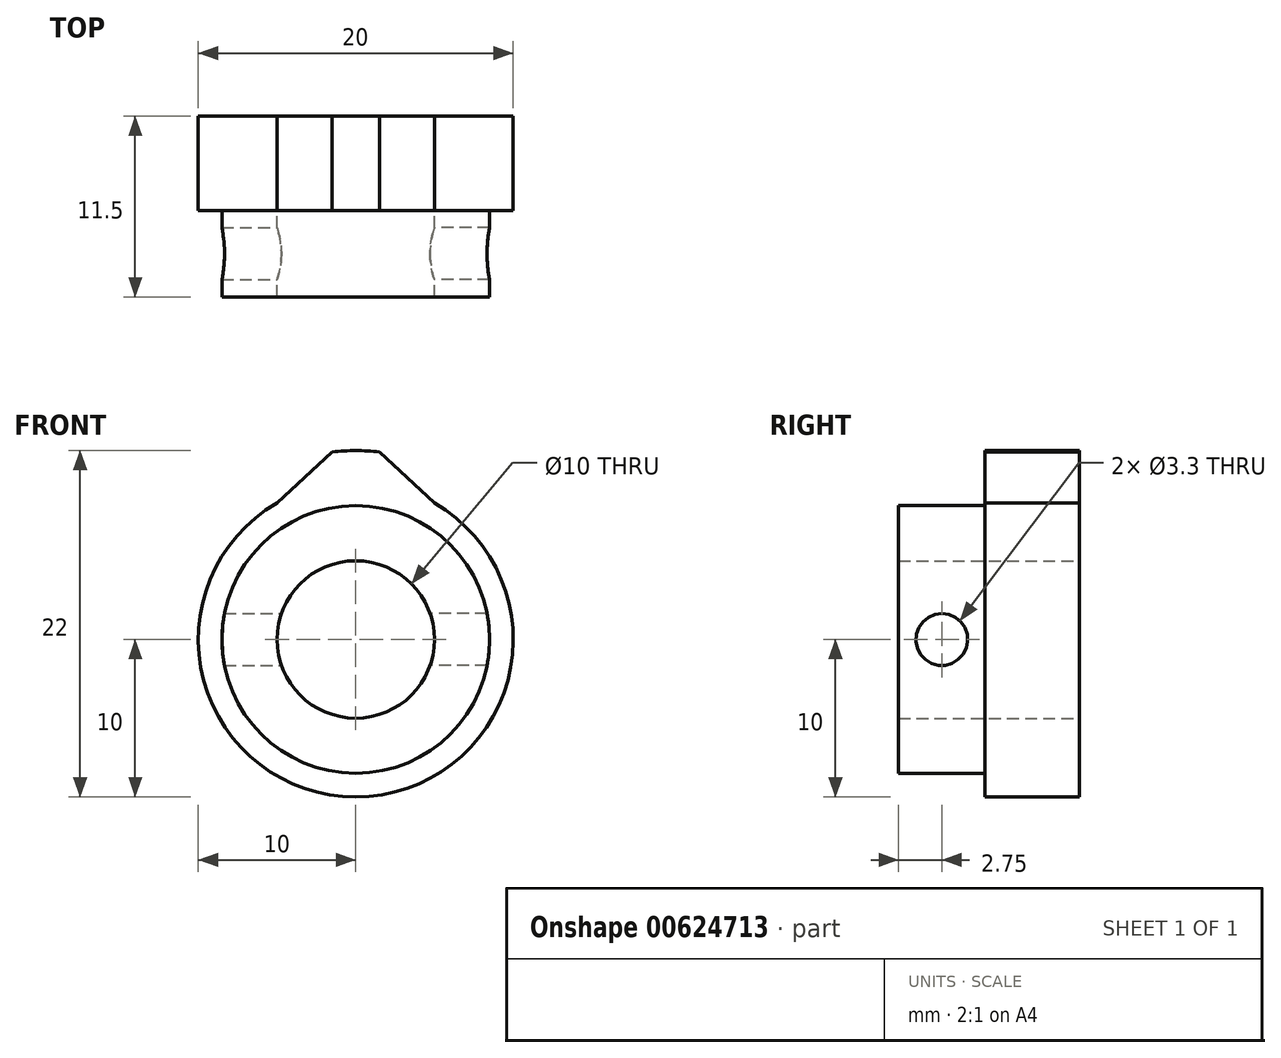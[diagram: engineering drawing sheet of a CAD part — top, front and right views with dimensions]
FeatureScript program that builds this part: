
annotation { "Feature Type Name" : "Feature", "Feature Type Description" : "" }
export const myFeature = defineFeature(function(context is Context, id is Id, definition is map)
    precondition{}
    {
        {
            var Q0;
            Q0=qCreatedBy(makeId("Front.planeOp"),FACE);
            var sketch = newSketch(context, id + "F0", { "sketchPlane" : qUnion([Q0])});
            skLineSegment(sketch, "E0", {"start": v(0, 53.33) * mm, "end": v(0, -48.13) * mm, "construction": true});
            skArc(sketch, "E1", {"start": v(-5, 8.66) * mm, "mid": v(0, -10) * mm, "end": v(5, 8.66) * mm});
            skArc(sketch, "E2", {"start": v(1.5, 11.9) * mm, "mid": v(0, 12) * mm, "end": v(-1.5, 11.9) * mm});
            skCircle(sketch, "E3", {"center": v(0, 0) * mm, "radius": 8.5 * mm});
            skCircle(sketch, "E4", {"center": v(0, 0) * mm, "radius": 5 * mm});
            skPoint(sketch, "E5", {"position": v(-5, 8.66) * mm});
            skPoint(sketch, "E6", {"position": v(5, 8.66) * mm});
            skPoint(sketch, "E7", {"position": v(-1.5, 11.9) * mm});
            skPoint(sketch, "E8", {"position": v(1.5, 11.9) * mm});
            skLineSegment(sketch, "E9", {"start": v(-1.5, 11.9) * mm, "end": v(-5, 8.66) * mm});
            skLineSegment(sketch, "E10", {"start": v(1.5, 11.9) * mm, "end": v(5, 8.66) * mm});
            skSolve(sketch);
        }
        {
            var Q0;
            Q0=makeQuery(id+"F0.imprint","IMPRINT",FACE,{"disambiguationData":[TD([[makeQuery(id+"F0.imprint","IMPRINT",EDGE,{"derivedFrom":sQuery(id+"F0.wireOp",EDGE,"E1")}),1.0]])]});
            var Q1;
            Q1=makeQuery(id+"F0.imprint","IMPRINT",FACE,{"disambiguationData":[TD([[makeQuery(id+"F0.imprint","IMPRINT",EDGE,{"derivedFrom":sQuery(id+"F0.wireOp",EDGE,"E3")}),1.0]])]});
            extrude(context, id + "F1", {"entities" : qUnion([Q0, Q1]), "depth" : 6 * mm, "offsetDistance" : 25 * mm});
        }
        {
            var Q0;
            Q0=makeQuery(id+"F0.imprint","IMPRINT",FACE,{"disambiguationData":[TD([[makeQuery(id+"F0.imprint","IMPRINT",EDGE,{"derivedFrom":sQuery(id+"F0.wireOp",EDGE,"E3")}),1.0]])]});
            extrude(context, id + "F2", {"entities" : qUnion([Q0]), "operationType" : NewBodyOperationType.ADD, "depth" : 11.5 * mm, "offsetDistance" : 25 * mm});
        }
        {
            var Q0;
            Q0=qCreatedBy(makeId("Right.planeOp"),FACE);
            var sketch = newSketch(context, id + "F3", { "sketchPlane" : qUnion([Q0])});
            skPoint(sketch, "E11", {"position": v(-8.75, 0) * mm});
            skSolve(sketch);
        }
        {
            var Q0;
            Q0=sQuery(id+"F3.wireOp",VERTEX,"E11");
            var Q1;
            Q1=makeQuery(id+"F1.opExtrude","SWEPT_BODY",BODY,{"disambiguationData":[OSD([sQuery(id+"F0.wireOp",EDGE,"E1"),sQuery(id+"F0.wireOp",EDGE,"E2"),sQuery(id+"F0.wireOp",EDGE,"E4"),sQuery(id+"F0.wireOp",EDGE,"E9"),sQuery(id+"F0.wireOp",EDGE,"E10")])]});
            hole(context, id + "F4", {"style" : HoleStyle.SIMPLE, "endStyle" : HoleEndStyle.THROUGH, "standardTappedOrClearance" : lookupTablePath({ "standard" : "ISO", "fit" : "Normal", "size" : "M3", "type" : "Clearance" }), "standardBlindInLast" : lookupTablePath({ "fit" : "Standard", "standard" : "ISO", "size" : "M3", "type" : "Clearance" }), "holeDiameter" : 3.3 * mm, "majorDiameter" : 5 * mm, "isTappedThrough" : true, "tappedDepth" : 12 * mm, "tapClearance" : 3, "locations" : qUnion([Q0]), "scope" : qUnion([Q1])});
        }
        {
            var Q0;
            Q0=sQuery(id+"F3.wireOp",VERTEX,"E11");
            var Q1;
            Q1=makeQuery(id+"F1.opExtrude","SWEPT_BODY",BODY,{"disambiguationData":[OSD([sQuery(id+"F0.wireOp",EDGE,"E1"),sQuery(id+"F0.wireOp",EDGE,"E2"),sQuery(id+"F0.wireOp",EDGE,"E4"),sQuery(id+"F0.wireOp",EDGE,"E9"),sQuery(id+"F0.wireOp",EDGE,"E10")])]});
            hole(context, id + "F5", {"style" : HoleStyle.SIMPLE, "endStyle" : HoleEndStyle.THROUGH, "oppositeDirection" : true, "standardTappedOrClearance" : lookupTablePath({ "standard" : "ISO", "fit" : "Normal", "size" : "M3", "type" : "Clearance" }), "standardBlindInLast" : lookupTablePath({ "fit" : "Standard", "standard" : "ISO", "size" : "M3", "type" : "Clearance" }), "holeDiameter" : 3.3 * mm, "majorDiameter" : 5 * mm, "isTappedThrough" : true, "tappedDepth" : 12 * mm, "tapClearance" : 3, "locations" : qUnion([Q0]), "scope" : qUnion([Q1])});
        }
    });
